# Revit family: Sanitary_Basins_AXOR_38010XXX-AXOR-Uno-Electronic-basin-mixer_
name_source: partatom
category: Plumbing Fixtures
revit_build: Autodesk Revit 2018 (Build: 20170223_1515(x64)
units: mm (PartAtom-declared; Revit-internal decimal feet)

## family parameters
Always vertical = No
Cut with Voids When Loaded = No
OmniClass Number = 23.45.00.00
OmniClass Title = Sanitary, Laundry, and Cleaning Equipment
Part Type = Normal
Room Calculation Point = No
Round Connector Dimension = Use Diameter
Shared = No
Work Plane-Based = Yes

## types (13) — shared parameters
Always visible = Yes
BIMobject category = Basins
Default Elevation = 1219 mm
Design country = Germany
EAN code = 4011097806518
Edition number = 1
GTIN code = https://4011097806518
IFC Classification = Sanitary Terminal
Installation instructions = https://www.axor-design.com
Manufacturer country = Germany
Manufacturer name = AXOR
Material main = Chrome
Product Guid = f9598156-de4c-4674-ba97-beba489c5812
Product SKU = 38010XXX
Product data url = https://www.bimobject.com
Product family = AXOR Uno
Product group = Electronic mixers
Product name = 38010XXX AXOR Uno Electronic basin mixer with temperature pre-adjustment with mains connection 230 V
Product url = https://www.axor-design.com
QR code = https://www.bimobject.com
Technical description = https://www.axor-design.com

## per-type parameters (varying)
| type | Material 1 |
| 000 Chrome | AXOR - AXOR One - 000 Chrome |
| 950 Brushed Brass | AXOR - AXOR One - 950 Brushed Brass |
| 140 Brushed Bronze | AXOR - AXOR One - 140 Brushed Bronze |
| 260 Brushed Chrome | AXOR - AXOR One - 260 Brushed Chrome |
| 250 Brushed Gold Optic | AXOR - AXOR One - 250 Brushed Gold Optic |
| 820 Brushed Nickel | AXOR - AXOR One - 820 Brushed Nickel |
| 670 Matte Black | AXOR - AXOR One - 670 Matte Black |
| 930 Polished Brass | AXOR - AXOR One - 930 Polished Brass |
| 130 Polished Bronze | AXOR - AXOR One - 130 Polished Bronze |
| 020 Polished Chrome | AXOR - AXOR One - 020 Polished Chrome |
| 990 Polished Gold Optic | AXOR - AXOR One - 990 Polished Gold Optic |
| 830 Polished Nickel | AXOR - AXOR One - 830 Polished Nickel |
| 800 Stainless Steel Optic | AXOR - AXOR One - 800 Stainless Steel Optic |

## geometry (parser evidence)
native form markers: Sweep x1
no freeform markers — native parametric forms only
